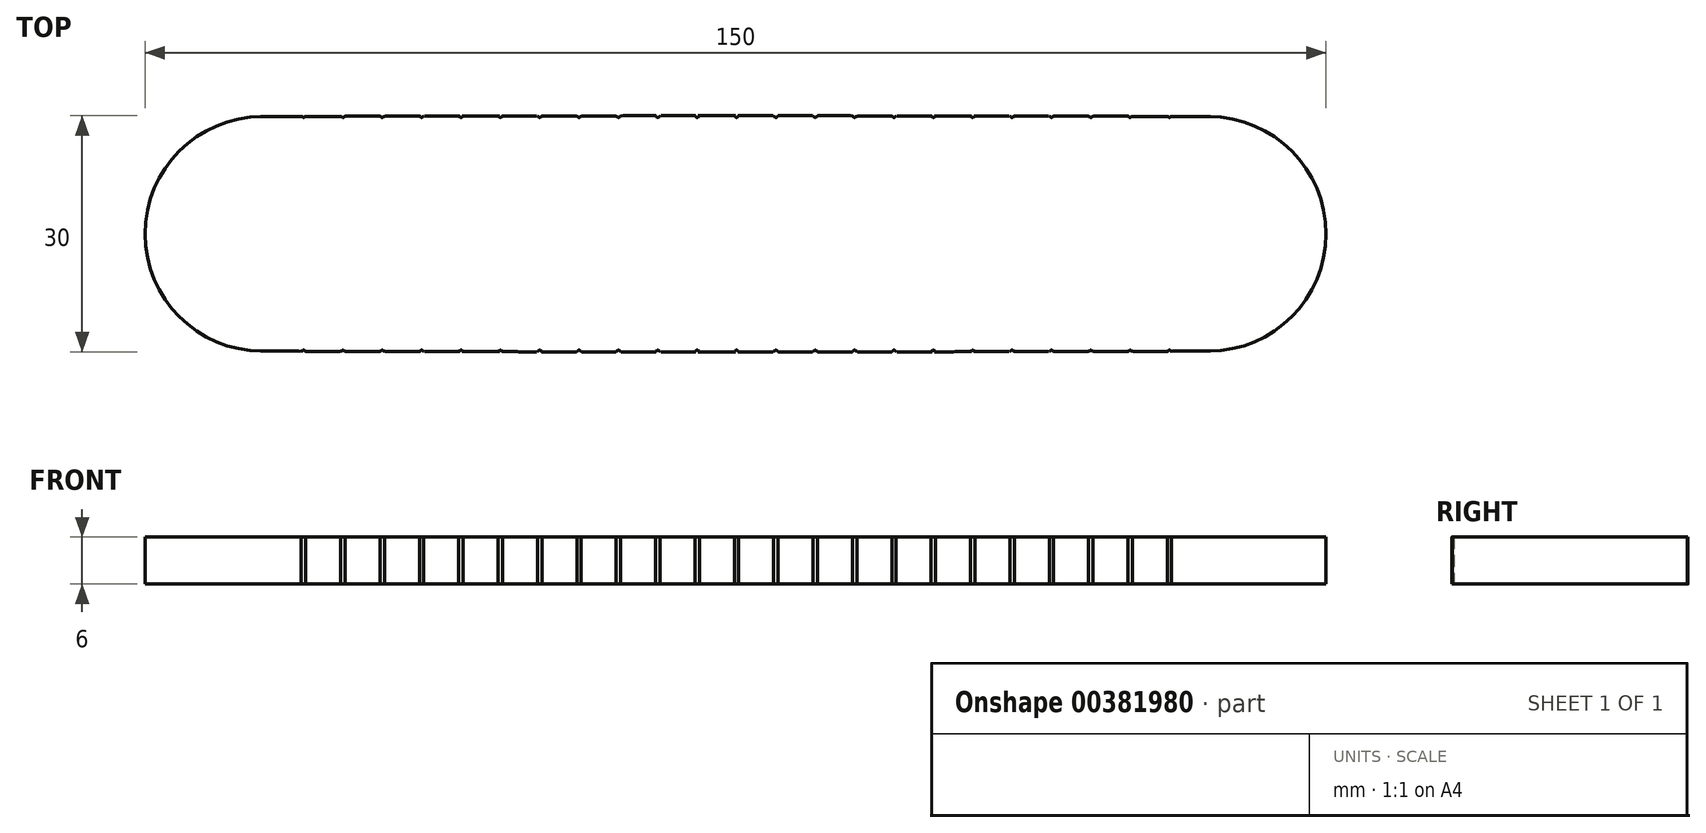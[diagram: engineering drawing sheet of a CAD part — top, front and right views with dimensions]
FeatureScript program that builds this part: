
annotation { "Feature Type Name" : "Feature", "Feature Type Description" : "" }
export const myFeature = defineFeature(function(context is Context, id is Id, definition is map)
    precondition{}
    {
        {
            var Q0;
            Q0=qCreatedBy(makeId("Top.planeOp"),FACE);
            var sketch = newSketch(context, id + "F0", { "sketchPlane" : qUnion([Q0])});
            skArc(sketch, "E0", {"start": v(0, 15) * mm, "mid": v(-30.07, 14.97) * mm, "end": v(-60.15, 14.9) * mm});
            skArc(sketch, "E1", {"start": v(-60.15, 14.9) * mm, "mid": v(-70.65, 10.52) * mm, "end": v(-75, 0) * mm});
            skLineSegment(sketch, "E2", {"start": v(0, 15) * mm, "end": v(78.08, 15) * mm, "construction": true});
            skLineSegment(sketch, "E3", {"start": v(0, 15) * mm, "end": v(0, -40.36) * mm, "construction": true});
            skLineSegment(sketch, "E4", {"start": v(-60.1, 0) * mm, "end": v(-3.88, 0) * mm, "construction": true});
            skArc(sketch, "E5.MirrorCS", {"start": v(0, 15) * mm, "mid": v(30.07, 14.97) * mm, "end": v(60.15, 14.9) * mm});
            skArc(sketch, "E6.MirrorCS", {"start": v(60.15, 14.9) * mm, "mid": v(70.65, 10.52) * mm, "end": v(75, 0) * mm});
            skArc(sketch, "E7.MirrorCS", {"start": v(0, -15) * mm, "mid": v(-30.07, -14.97) * mm, "end": v(-60.15, -14.9) * mm});
            skArc(sketch, "E8.MirrorCS", {"start": v(0, -15) * mm, "mid": v(30.07, -14.97) * mm, "end": v(60.15, -14.9) * mm});
            skArc(sketch, "E9.MirrorCS", {"start": v(60.15, -14.9) * mm, "mid": v(70.65, -10.52) * mm, "end": v(75, 0) * mm});
            skArc(sketch, "E10.MirrorCS", {"start": v(-60.15, -14.9) * mm, "mid": v(-70.65, -10.52) * mm, "end": v(-75, 0) * mm});
            skSolve(sketch);
        }
        {
            var Q0;
            Q0 = qSketchRegion(id + "F0", true);
            extrude(context, id + "F1", {"entities" : qUnion([Q0]), "depth" : 6 * mm});
        }
        {
            var Q0;
            Q0=qCreatedBy(makeId("Top.planeOp"),FACE);
            var sketch = newSketch(context, id + "F2", { "sketchPlane" : qUnion([Q0])});
            skArc(sketch, "E11", {"start": v(-54.93, 14.8) * mm, "mid": v(-55.03, 14.87) * mm, "end": v(-55.15, 14.9) * mm});
            skArc(sketch, "E12", {"start": v(-54.93, 14.8) * mm, "mid": v(-54.87, 14.77) * mm, "end": v(-54.81, 14.8) * mm});
            skArc(sketch, "E13", {"start": v(-54.81, 14.8) * mm, "mid": v(-54.71, 14.87) * mm, "end": v(-54.6, 14.9) * mm});
            skLineSegment(sketch, "E14", {"start": v(-55.15, 14.9) * mm, "end": v(-49.73, 14.9) * mm, "construction": true});
            skLineSegment(sketch, "E15", {"start": v(-54.6, 14.9) * mm, "end": v(-47.2, 14.9) * mm, "construction": true});
            skLineSegment(sketch, "E16", {"start": v(-55.15, 14.9) * mm, "end": v(-55.15, 15.28) * mm});
            skLineSegment(sketch, "E17", {"start": v(-55.15, 15.28) * mm, "end": v(-54.6, 15.28) * mm});
            skLineSegment(sketch, "E18", {"start": v(-54.6, 15.28) * mm, "end": v(-54.6, 14.9) * mm});
            skArc(sketch, "E19.MirrorCS", {"start": v(-54.93, -14.8) * mm, "mid": v(-55.03, -14.87) * mm, "end": v(-55.15, -14.9) * mm});
            skArc(sketch, "E20.MirrorCS", {"start": v(-54.93, -14.8) * mm, "mid": v(-54.87, -14.77) * mm, "end": v(-54.81, -14.8) * mm});
            skArc(sketch, "E21.MirrorCS", {"start": v(-54.81, -14.8) * mm, "mid": v(-54.71, -14.87) * mm, "end": v(-54.6, -14.9) * mm});
            skLineSegment(sketch, "E22.MirrorCS", {"start": v(-55.15, -14.9) * mm, "end": v(-55.15, -15.28) * mm});
            skLineSegment(sketch, "E23.MirrorCS", {"start": v(-55.15, -15.28) * mm, "end": v(-54.6, -15.28) * mm});
            skLineSegment(sketch, "E24.MirrorCS", {"start": v(-54.6, -15.28) * mm, "end": v(-54.6, -14.9) * mm});
            skLineSegment(sketch, "E25.1.0.0", {"start": v(-50.15, -15.28) * mm, "end": v(-49.6, -15.28) * mm});
            skLineSegment(sketch, "E25.1.0.1", {"start": v(-49.6, -15.28) * mm, "end": v(-49.6, -14.9) * mm});
            skLineSegment(sketch, "E25.1.0.2", {"start": v(-50.15, -14.9) * mm, "end": v(-50.15, -15.28) * mm});
            skArc(sketch, "E25.1.0.3", {"start": v(-49.81, -14.8) * mm, "mid": v(-49.71, -14.87) * mm, "end": v(-49.6, -14.9) * mm});
            skArc(sketch, "E25.1.0.4", {"start": v(-49.93, -14.8) * mm, "mid": v(-49.87, -14.77) * mm, "end": v(-49.81, -14.8) * mm});
            skArc(sketch, "E25.1.0.5", {"start": v(-49.93, 14.8) * mm, "mid": v(-50.03, 14.87) * mm, "end": v(-50.15, 14.9) * mm});
            skArc(sketch, "E25.1.0.6", {"start": v(-49.93, 14.8) * mm, "mid": v(-49.87, 14.77) * mm, "end": v(-49.81, 14.8) * mm});
            skArc(sketch, "E25.1.0.7", {"start": v(-49.81, 14.8) * mm, "mid": v(-49.71, 14.87) * mm, "end": v(-49.6, 14.9) * mm});
            skArc(sketch, "E25.1.0.8", {"start": v(-49.93, -14.8) * mm, "mid": v(-50.03, -14.87) * mm, "end": v(-50.15, -14.9) * mm});
            skLineSegment(sketch, "E25.1.0.9", {"start": v(-49.6, 15.28) * mm, "end": v(-49.6, 14.9) * mm});
            skLineSegment(sketch, "E25.1.0.10", {"start": v(-50.15, 14.9) * mm, "end": v(-50.15, 15.28) * mm});
            skLineSegment(sketch, "E25.1.0.11", {"start": v(-50.15, 15.28) * mm, "end": v(-49.6, 15.28) * mm});
            skLineSegment(sketch, "E25.2.0.0", {"start": v(-45.15, -15.28) * mm, "end": v(-44.6, -15.28) * mm});
            skLineSegment(sketch, "E25.2.0.1", {"start": v(-44.6, -15.28) * mm, "end": v(-44.6, -14.9) * mm});
            skLineSegment(sketch, "E25.2.0.2", {"start": v(-45.15, -14.9) * mm, "end": v(-45.15, -15.28) * mm});
            skArc(sketch, "E25.2.0.3", {"start": v(-44.81, -14.8) * mm, "mid": v(-44.71, -14.87) * mm, "end": v(-44.6, -14.9) * mm});
            skArc(sketch, "E25.2.0.4", {"start": v(-44.93, -14.8) * mm, "mid": v(-44.87, -14.77) * mm, "end": v(-44.81, -14.8) * mm});
            skArc(sketch, "E25.2.0.5", {"start": v(-44.93, 14.8) * mm, "mid": v(-45.03, 14.87) * mm, "end": v(-45.15, 14.9) * mm});
            skArc(sketch, "E25.2.0.6", {"start": v(-44.93, 14.8) * mm, "mid": v(-44.87, 14.77) * mm, "end": v(-44.81, 14.8) * mm});
            skArc(sketch, "E25.2.0.7", {"start": v(-44.81, 14.8) * mm, "mid": v(-44.71, 14.87) * mm, "end": v(-44.6, 14.9) * mm});
            skArc(sketch, "E25.2.0.8", {"start": v(-44.93, -14.8) * mm, "mid": v(-45.03, -14.87) * mm, "end": v(-45.15, -14.9) * mm});
            skLineSegment(sketch, "E25.2.0.9", {"start": v(-44.6, 15.28) * mm, "end": v(-44.6, 14.9) * mm});
            skLineSegment(sketch, "E25.2.0.10", {"start": v(-45.15, 14.9) * mm, "end": v(-45.15, 15.28) * mm});
            skLineSegment(sketch, "E25.2.0.11", {"start": v(-45.15, 15.28) * mm, "end": v(-44.6, 15.28) * mm});
            skLineSegment(sketch, "E25.3.0.0", {"start": v(-40.15, -15.28) * mm, "end": v(-39.6, -15.28) * mm});
            skLineSegment(sketch, "E25.3.0.1", {"start": v(-39.6, -15.28) * mm, "end": v(-39.6, -14.9) * mm});
            skLineSegment(sketch, "E25.3.0.2", {"start": v(-40.15, -14.9) * mm, "end": v(-40.15, -15.28) * mm});
            skArc(sketch, "E25.3.0.3", {"start": v(-39.81, -14.8) * mm, "mid": v(-39.71, -14.87) * mm, "end": v(-39.6, -14.9) * mm});
            skArc(sketch, "E25.3.0.4", {"start": v(-39.93, -14.8) * mm, "mid": v(-39.87, -14.77) * mm, "end": v(-39.81, -14.8) * mm});
            skArc(sketch, "E25.3.0.5", {"start": v(-39.93, 14.8) * mm, "mid": v(-40.03, 14.87) * mm, "end": v(-40.15, 14.9) * mm});
            skArc(sketch, "E25.3.0.6", {"start": v(-39.93, 14.8) * mm, "mid": v(-39.87, 14.77) * mm, "end": v(-39.81, 14.8) * mm});
            skArc(sketch, "E25.3.0.7", {"start": v(-39.81, 14.8) * mm, "mid": v(-39.71, 14.87) * mm, "end": v(-39.6, 14.9) * mm});
            skArc(sketch, "E25.3.0.8", {"start": v(-39.93, -14.8) * mm, "mid": v(-40.03, -14.87) * mm, "end": v(-40.15, -14.9) * mm});
            skLineSegment(sketch, "E25.3.0.9", {"start": v(-39.6, 15.28) * mm, "end": v(-39.6, 14.9) * mm});
            skLineSegment(sketch, "E25.3.0.10", {"start": v(-40.15, 14.9) * mm, "end": v(-40.15, 15.28) * mm});
            skLineSegment(sketch, "E25.3.0.11", {"start": v(-40.15, 15.28) * mm, "end": v(-39.6, 15.28) * mm});
            skLineSegment(sketch, "E25.4.0.0", {"start": v(-35.15, -15.28) * mm, "end": v(-34.6, -15.28) * mm});
            skLineSegment(sketch, "E25.4.0.1", {"start": v(-34.6, -15.28) * mm, "end": v(-34.6, -14.9) * mm});
            skLineSegment(sketch, "E25.4.0.2", {"start": v(-35.15, -14.9) * mm, "end": v(-35.15, -15.28) * mm});
            skArc(sketch, "E25.4.0.3", {"start": v(-34.81, -14.8) * mm, "mid": v(-34.71, -14.87) * mm, "end": v(-34.6, -14.9) * mm});
            skArc(sketch, "E25.4.0.4", {"start": v(-34.93, -14.8) * mm, "mid": v(-34.87, -14.77) * mm, "end": v(-34.81, -14.8) * mm});
            skArc(sketch, "E25.4.0.5", {"start": v(-34.93, 14.8) * mm, "mid": v(-35.03, 14.87) * mm, "end": v(-35.15, 14.9) * mm});
            skArc(sketch, "E25.4.0.6", {"start": v(-34.93, 14.8) * mm, "mid": v(-34.87, 14.77) * mm, "end": v(-34.81, 14.8) * mm});
            skArc(sketch, "E25.4.0.7", {"start": v(-34.81, 14.8) * mm, "mid": v(-34.71, 14.87) * mm, "end": v(-34.6, 14.9) * mm});
            skArc(sketch, "E25.4.0.8", {"start": v(-34.93, -14.8) * mm, "mid": v(-35.03, -14.87) * mm, "end": v(-35.15, -14.9) * mm});
            skLineSegment(sketch, "E25.4.0.9", {"start": v(-34.6, 15.28) * mm, "end": v(-34.6, 14.9) * mm});
            skLineSegment(sketch, "E25.4.0.10", {"start": v(-35.15, 14.9) * mm, "end": v(-35.15, 15.28) * mm});
            skLineSegment(sketch, "E25.4.0.11", {"start": v(-35.15, 15.28) * mm, "end": v(-34.6, 15.28) * mm});
            skLineSegment(sketch, "E25.5.0.0", {"start": v(-30.15, -15.28) * mm, "end": v(-29.6, -15.28) * mm});
            skLineSegment(sketch, "E25.5.0.1", {"start": v(-29.6, -15.28) * mm, "end": v(-29.6, -14.9) * mm});
            skLineSegment(sketch, "E25.5.0.2", {"start": v(-30.15, -14.9) * mm, "end": v(-30.15, -15.28) * mm});
            skArc(sketch, "E25.5.0.3", {"start": v(-29.81, -14.8) * mm, "mid": v(-29.71, -14.87) * mm, "end": v(-29.6, -14.9) * mm});
            skArc(sketch, "E25.5.0.4", {"start": v(-29.93, -14.8) * mm, "mid": v(-29.87, -14.77) * mm, "end": v(-29.81, -14.8) * mm});
            skArc(sketch, "E25.5.0.5", {"start": v(-29.93, 14.8) * mm, "mid": v(-30.03, 14.87) * mm, "end": v(-30.15, 14.9) * mm});
            skArc(sketch, "E25.5.0.6", {"start": v(-29.93, 14.8) * mm, "mid": v(-29.87, 14.77) * mm, "end": v(-29.81, 14.8) * mm});
            skArc(sketch, "E25.5.0.7", {"start": v(-29.81, 14.8) * mm, "mid": v(-29.71, 14.87) * mm, "end": v(-29.6, 14.9) * mm});
            skArc(sketch, "E25.5.0.8", {"start": v(-29.93, -14.8) * mm, "mid": v(-30.03, -14.87) * mm, "end": v(-30.15, -14.9) * mm});
            skLineSegment(sketch, "E25.5.0.9", {"start": v(-29.6, 15.28) * mm, "end": v(-29.6, 14.9) * mm});
            skLineSegment(sketch, "E25.5.0.10", {"start": v(-30.15, 14.9) * mm, "end": v(-30.15, 15.28) * mm});
            skLineSegment(sketch, "E25.5.0.11", {"start": v(-30.15, 15.28) * mm, "end": v(-29.6, 15.28) * mm});
            skLineSegment(sketch, "E25.6.0.0", {"start": v(-25.15, -15.28) * mm, "end": v(-24.6, -15.28) * mm});
            skLineSegment(sketch, "E25.6.0.1", {"start": v(-24.6, -15.28) * mm, "end": v(-24.6, -14.9) * mm});
            skLineSegment(sketch, "E25.6.0.2", {"start": v(-25.15, -14.9) * mm, "end": v(-25.15, -15.28) * mm});
            skArc(sketch, "E25.6.0.3", {"start": v(-24.81, -14.8) * mm, "mid": v(-24.71, -14.87) * mm, "end": v(-24.6, -14.9) * mm});
            skArc(sketch, "E25.6.0.4", {"start": v(-24.93, -14.8) * mm, "mid": v(-24.87, -14.77) * mm, "end": v(-24.81, -14.8) * mm});
            skArc(sketch, "E25.6.0.5", {"start": v(-24.93, 14.8) * mm, "mid": v(-25.03, 14.87) * mm, "end": v(-25.15, 14.9) * mm});
            skArc(sketch, "E25.6.0.6", {"start": v(-24.93, 14.8) * mm, "mid": v(-24.87, 14.77) * mm, "end": v(-24.81, 14.8) * mm});
            skArc(sketch, "E25.6.0.7", {"start": v(-24.81, 14.8) * mm, "mid": v(-24.71, 14.87) * mm, "end": v(-24.6, 14.9) * mm});
            skArc(sketch, "E25.6.0.8", {"start": v(-24.93, -14.8) * mm, "mid": v(-25.03, -14.87) * mm, "end": v(-25.15, -14.9) * mm});
            skLineSegment(sketch, "E25.6.0.9", {"start": v(-24.6, 15.28) * mm, "end": v(-24.6, 14.9) * mm});
            skLineSegment(sketch, "E25.6.0.10", {"start": v(-25.15, 14.9) * mm, "end": v(-25.15, 15.28) * mm});
            skLineSegment(sketch, "E25.6.0.11", {"start": v(-25.15, 15.28) * mm, "end": v(-24.6, 15.28) * mm});
            skLineSegment(sketch, "E25.7.0.0", {"start": v(-20.15, -15.28) * mm, "end": v(-19.6, -15.28) * mm});
            skLineSegment(sketch, "E25.7.0.1", {"start": v(-19.6, -15.28) * mm, "end": v(-19.6, -14.9) * mm});
            skLineSegment(sketch, "E25.7.0.2", {"start": v(-20.15, -14.9) * mm, "end": v(-20.15, -15.28) * mm});
            skArc(sketch, "E25.7.0.3", {"start": v(-19.81, -14.8) * mm, "mid": v(-19.71, -14.87) * mm, "end": v(-19.6, -14.9) * mm});
            skArc(sketch, "E25.7.0.4", {"start": v(-19.93, -14.8) * mm, "mid": v(-19.87, -14.77) * mm, "end": v(-19.81, -14.8) * mm});
            skArc(sketch, "E25.7.0.5", {"start": v(-19.93, 14.8) * mm, "mid": v(-20.03, 14.87) * mm, "end": v(-20.15, 14.9) * mm});
            skArc(sketch, "E25.7.0.6", {"start": v(-19.93, 14.8) * mm, "mid": v(-19.87, 14.77) * mm, "end": v(-19.81, 14.8) * mm});
            skArc(sketch, "E25.7.0.7", {"start": v(-19.81, 14.8) * mm, "mid": v(-19.71, 14.87) * mm, "end": v(-19.6, 14.9) * mm});
            skArc(sketch, "E25.7.0.8", {"start": v(-19.93, -14.8) * mm, "mid": v(-20.03, -14.87) * mm, "end": v(-20.15, -14.9) * mm});
            skLineSegment(sketch, "E25.7.0.9", {"start": v(-19.6, 15.28) * mm, "end": v(-19.6, 14.9) * mm});
            skLineSegment(sketch, "E25.7.0.10", {"start": v(-20.15, 14.9) * mm, "end": v(-20.15, 15.28) * mm});
            skLineSegment(sketch, "E25.7.0.11", {"start": v(-20.15, 15.28) * mm, "end": v(-19.6, 15.28) * mm});
            skLineSegment(sketch, "E25.8.0.0", {"start": v(-15.15, -15.28) * mm, "end": v(-14.6, -15.28) * mm});
            skLineSegment(sketch, "E25.8.0.1", {"start": v(-14.6, -15.28) * mm, "end": v(-14.6, -14.9) * mm});
            skLineSegment(sketch, "E25.8.0.2", {"start": v(-15.15, -14.9) * mm, "end": v(-15.15, -15.28) * mm});
            skArc(sketch, "E25.8.0.3", {"start": v(-14.81, -14.8) * mm, "mid": v(-14.71, -14.87) * mm, "end": v(-14.6, -14.9) * mm});
            skArc(sketch, "E25.8.0.4", {"start": v(-14.93, -14.8) * mm, "mid": v(-14.87, -14.77) * mm, "end": v(-14.81, -14.8) * mm});
            skArc(sketch, "E25.8.0.5", {"start": v(-14.93, 14.8) * mm, "mid": v(-15.03, 14.87) * mm, "end": v(-15.15, 14.9) * mm});
            skArc(sketch, "E25.8.0.6", {"start": v(-14.93, 14.8) * mm, "mid": v(-14.87, 14.77) * mm, "end": v(-14.81, 14.8) * mm});
            skArc(sketch, "E25.8.0.7", {"start": v(-14.81, 14.8) * mm, "mid": v(-14.71, 14.87) * mm, "end": v(-14.6, 14.9) * mm});
            skArc(sketch, "E25.8.0.8", {"start": v(-14.93, -14.8) * mm, "mid": v(-15.03, -14.87) * mm, "end": v(-15.15, -14.9) * mm});
            skLineSegment(sketch, "E25.8.0.9", {"start": v(-14.6, 15.28) * mm, "end": v(-14.6, 14.9) * mm});
            skLineSegment(sketch, "E25.8.0.10", {"start": v(-15.15, 14.9) * mm, "end": v(-15.15, 15.28) * mm});
            skLineSegment(sketch, "E25.8.0.11", {"start": v(-15.15, 15.28) * mm, "end": v(-14.6, 15.28) * mm});
            skLineSegment(sketch, "E25.9.0.0", {"start": v(-10.15, -15.28) * mm, "end": v(-9.6, -15.28) * mm});
            skLineSegment(sketch, "E25.9.0.1", {"start": v(-9.6, -15.28) * mm, "end": v(-9.6, -14.9) * mm});
            skLineSegment(sketch, "E25.9.0.2", {"start": v(-10.15, -14.9) * mm, "end": v(-10.15, -15.28) * mm});
            skArc(sketch, "E25.9.0.3", {"start": v(-9.81, -14.8) * mm, "mid": v(-9.71, -14.87) * mm, "end": v(-9.6, -14.9) * mm});
            skArc(sketch, "E25.9.0.4", {"start": v(-9.93, -14.8) * mm, "mid": v(-9.87, -14.77) * mm, "end": v(-9.81, -14.8) * mm});
            skArc(sketch, "E25.9.0.5", {"start": v(-9.93, 14.8) * mm, "mid": v(-10.03, 14.87) * mm, "end": v(-10.15, 14.9) * mm});
            skArc(sketch, "E25.9.0.6", {"start": v(-9.93, 14.8) * mm, "mid": v(-9.87, 14.77) * mm, "end": v(-9.81, 14.8) * mm});
            skArc(sketch, "E25.9.0.7", {"start": v(-9.81, 14.8) * mm, "mid": v(-9.71, 14.87) * mm, "end": v(-9.6, 14.9) * mm});
            skArc(sketch, "E25.9.0.8", {"start": v(-9.93, -14.8) * mm, "mid": v(-10.03, -14.87) * mm, "end": v(-10.15, -14.9) * mm});
            skLineSegment(sketch, "E25.9.0.9", {"start": v(-9.6, 15.28) * mm, "end": v(-9.6, 14.9) * mm});
            skLineSegment(sketch, "E25.9.0.10", {"start": v(-10.15, 14.9) * mm, "end": v(-10.15, 15.28) * mm});
            skLineSegment(sketch, "E25.9.0.11", {"start": v(-10.15, 15.28) * mm, "end": v(-9.6, 15.28) * mm});
            skLineSegment(sketch, "E25.10.0.0", {"start": v(-5.15, -15.28) * mm, "end": v(-4.6, -15.28) * mm});
            skLineSegment(sketch, "E25.10.0.1", {"start": v(-4.6, -15.28) * mm, "end": v(-4.6, -14.9) * mm});
            skLineSegment(sketch, "E25.10.0.2", {"start": v(-5.15, -14.9) * mm, "end": v(-5.15, -15.28) * mm});
            skArc(sketch, "E25.10.0.3", {"start": v(-4.81, -14.8) * mm, "mid": v(-4.71, -14.87) * mm, "end": v(-4.6, -14.9) * mm});
            skArc(sketch, "E25.10.0.4", {"start": v(-4.93, -14.8) * mm, "mid": v(-4.87, -14.77) * mm, "end": v(-4.81, -14.8) * mm});
            skArc(sketch, "E25.10.0.5", {"start": v(-4.93, 14.8) * mm, "mid": v(-5.03, 14.87) * mm, "end": v(-5.15, 14.9) * mm});
            skArc(sketch, "E25.10.0.6", {"start": v(-4.93, 14.8) * mm, "mid": v(-4.87, 14.77) * mm, "end": v(-4.81, 14.8) * mm});
            skArc(sketch, "E25.10.0.7", {"start": v(-4.81, 14.8) * mm, "mid": v(-4.71, 14.87) * mm, "end": v(-4.6, 14.9) * mm});
            skArc(sketch, "E25.10.0.8", {"start": v(-4.93, -14.8) * mm, "mid": v(-5.03, -14.87) * mm, "end": v(-5.15, -14.9) * mm});
            skLineSegment(sketch, "E25.10.0.9", {"start": v(-4.6, 15.28) * mm, "end": v(-4.6, 14.9) * mm});
            skLineSegment(sketch, "E25.10.0.10", {"start": v(-5.15, 14.9) * mm, "end": v(-5.15, 15.28) * mm});
            skLineSegment(sketch, "E25.10.0.11", {"start": v(-5.15, 15.28) * mm, "end": v(-4.6, 15.28) * mm});
            skLineSegment(sketch, "E25.11.0.0", {"start": v(-0.15, -15.28) * mm, "end": v(0.4, -15.28) * mm});
            skLineSegment(sketch, "E25.11.0.1", {"start": v(0.4, -15.28) * mm, "end": v(0.4, -14.9) * mm});
            skLineSegment(sketch, "E25.11.0.2", {"start": v(-0.15, -14.9) * mm, "end": v(-0.15, -15.28) * mm});
            skArc(sketch, "E25.11.0.3", {"start": v(0.19, -14.8) * mm, "mid": v(0.29, -14.87) * mm, "end": v(0.4, -14.9) * mm});
            skArc(sketch, "E25.11.0.4", {"start": v(0.07, -14.8) * mm, "mid": v(0.13, -14.77) * mm, "end": v(0.19, -14.8) * mm});
            skArc(sketch, "E25.11.0.5", {"start": v(0.07, 14.8) * mm, "mid": v(-0.03, 14.87) * mm, "end": v(-0.15, 14.9) * mm});
            skArc(sketch, "E25.11.0.6", {"start": v(0.07, 14.8) * mm, "mid": v(0.13, 14.77) * mm, "end": v(0.19, 14.8) * mm});
            skArc(sketch, "E25.11.0.7", {"start": v(0.19, 14.8) * mm, "mid": v(0.29, 14.87) * mm, "end": v(0.4, 14.9) * mm});
            skArc(sketch, "E25.11.0.8", {"start": v(0.07, -14.8) * mm, "mid": v(-0.03, -14.87) * mm, "end": v(-0.15, -14.9) * mm});
            skLineSegment(sketch, "E25.11.0.9", {"start": v(0.4, 15.28) * mm, "end": v(0.4, 14.9) * mm});
            skLineSegment(sketch, "E25.11.0.10", {"start": v(-0.15, 14.9) * mm, "end": v(-0.15, 15.28) * mm});
            skLineSegment(sketch, "E25.11.0.11", {"start": v(-0.15, 15.28) * mm, "end": v(0.4, 15.28) * mm});
            skLineSegment(sketch, "E25.12.0.0", {"start": v(4.85, -15.28) * mm, "end": v(5.4, -15.28) * mm});
            skLineSegment(sketch, "E25.12.0.1", {"start": v(5.4, -15.28) * mm, "end": v(5.4, -14.9) * mm});
            skLineSegment(sketch, "E25.12.0.2", {"start": v(4.85, -14.9) * mm, "end": v(4.85, -15.28) * mm});
            skArc(sketch, "E25.12.0.3", {"start": v(5.19, -14.8) * mm, "mid": v(5.29, -14.87) * mm, "end": v(5.4, -14.9) * mm});
            skArc(sketch, "E25.12.0.4", {"start": v(5.07, -14.8) * mm, "mid": v(5.13, -14.77) * mm, "end": v(5.19, -14.8) * mm});
            skArc(sketch, "E25.12.0.5", {"start": v(5.07, 14.8) * mm, "mid": v(4.97, 14.87) * mm, "end": v(4.85, 14.9) * mm});
            skArc(sketch, "E25.12.0.6", {"start": v(5.07, 14.8) * mm, "mid": v(5.13, 14.77) * mm, "end": v(5.19, 14.8) * mm});
            skArc(sketch, "E25.12.0.7", {"start": v(5.19, 14.8) * mm, "mid": v(5.29, 14.87) * mm, "end": v(5.4, 14.9) * mm});
            skArc(sketch, "E25.12.0.8", {"start": v(5.07, -14.8) * mm, "mid": v(4.97, -14.87) * mm, "end": v(4.85, -14.9) * mm});
            skLineSegment(sketch, "E25.12.0.9", {"start": v(5.4, 15.28) * mm, "end": v(5.4, 14.9) * mm});
            skLineSegment(sketch, "E25.12.0.10", {"start": v(4.85, 14.9) * mm, "end": v(4.85, 15.28) * mm});
            skLineSegment(sketch, "E25.12.0.11", {"start": v(4.85, 15.28) * mm, "end": v(5.4, 15.28) * mm});
            skLineSegment(sketch, "E25.13.0.0", {"start": v(9.85, -15.28) * mm, "end": v(10.4, -15.28) * mm});
            skLineSegment(sketch, "E25.13.0.1", {"start": v(10.4, -15.28) * mm, "end": v(10.4, -14.9) * mm});
            skLineSegment(sketch, "E25.13.0.2", {"start": v(9.85, -14.9) * mm, "end": v(9.85, -15.28) * mm});
            skArc(sketch, "E25.13.0.3", {"start": v(10.19, -14.8) * mm, "mid": v(10.29, -14.87) * mm, "end": v(10.4, -14.9) * mm});
            skArc(sketch, "E25.13.0.4", {"start": v(10.07, -14.8) * mm, "mid": v(10.13, -14.77) * mm, "end": v(10.19, -14.8) * mm});
            skArc(sketch, "E25.13.0.5", {"start": v(10.07, 14.8) * mm, "mid": v(9.97, 14.87) * mm, "end": v(9.85, 14.9) * mm});
            skArc(sketch, "E25.13.0.6", {"start": v(10.07, 14.8) * mm, "mid": v(10.13, 14.77) * mm, "end": v(10.19, 14.8) * mm});
            skArc(sketch, "E25.13.0.7", {"start": v(10.19, 14.8) * mm, "mid": v(10.29, 14.87) * mm, "end": v(10.4, 14.9) * mm});
            skArc(sketch, "E25.13.0.8", {"start": v(10.07, -14.8) * mm, "mid": v(9.97, -14.87) * mm, "end": v(9.85, -14.9) * mm});
            skLineSegment(sketch, "E25.13.0.9", {"start": v(10.4, 15.28) * mm, "end": v(10.4, 14.9) * mm});
            skLineSegment(sketch, "E25.13.0.10", {"start": v(9.85, 14.9) * mm, "end": v(9.85, 15.28) * mm});
            skLineSegment(sketch, "E25.13.0.11", {"start": v(9.85, 15.28) * mm, "end": v(10.4, 15.28) * mm});
            skLineSegment(sketch, "E25.14.0.0", {"start": v(14.85, -15.28) * mm, "end": v(15.4, -15.28) * mm});
            skLineSegment(sketch, "E25.14.0.1", {"start": v(15.4, -15.28) * mm, "end": v(15.4, -14.9) * mm});
            skLineSegment(sketch, "E25.14.0.2", {"start": v(14.85, -14.9) * mm, "end": v(14.85, -15.28) * mm});
            skArc(sketch, "E25.14.0.3", {"start": v(15.19, -14.8) * mm, "mid": v(15.29, -14.87) * mm, "end": v(15.4, -14.9) * mm});
            skArc(sketch, "E25.14.0.4", {"start": v(15.07, -14.8) * mm, "mid": v(15.13, -14.77) * mm, "end": v(15.19, -14.8) * mm});
            skArc(sketch, "E25.14.0.5", {"start": v(15.07, 14.8) * mm, "mid": v(14.97, 14.87) * mm, "end": v(14.85, 14.9) * mm});
            skArc(sketch, "E25.14.0.6", {"start": v(15.07, 14.8) * mm, "mid": v(15.13, 14.77) * mm, "end": v(15.19, 14.8) * mm});
            skArc(sketch, "E25.14.0.7", {"start": v(15.19, 14.8) * mm, "mid": v(15.29, 14.87) * mm, "end": v(15.4, 14.9) * mm});
            skArc(sketch, "E25.14.0.8", {"start": v(15.07, -14.8) * mm, "mid": v(14.97, -14.87) * mm, "end": v(14.85, -14.9) * mm});
            skLineSegment(sketch, "E25.14.0.9", {"start": v(15.4, 15.28) * mm, "end": v(15.4, 14.9) * mm});
            skLineSegment(sketch, "E25.14.0.10", {"start": v(14.85, 14.9) * mm, "end": v(14.85, 15.28) * mm});
            skLineSegment(sketch, "E25.14.0.11", {"start": v(14.85, 15.28) * mm, "end": v(15.4, 15.28) * mm});
            skLineSegment(sketch, "E25.15.0.0", {"start": v(19.85, -15.28) * mm, "end": v(20.4, -15.28) * mm});
            skLineSegment(sketch, "E25.15.0.1", {"start": v(20.4, -15.28) * mm, "end": v(20.4, -14.9) * mm});
            skLineSegment(sketch, "E25.15.0.2", {"start": v(19.85, -14.9) * mm, "end": v(19.85, -15.28) * mm});
            skArc(sketch, "E25.15.0.3", {"start": v(20.19, -14.8) * mm, "mid": v(20.29, -14.87) * mm, "end": v(20.4, -14.9) * mm});
            skArc(sketch, "E25.15.0.4", {"start": v(20.07, -14.8) * mm, "mid": v(20.13, -14.77) * mm, "end": v(20.19, -14.8) * mm});
            skArc(sketch, "E25.15.0.5", {"start": v(20.07, 14.8) * mm, "mid": v(19.97, 14.87) * mm, "end": v(19.85, 14.9) * mm});
            skArc(sketch, "E25.15.0.6", {"start": v(20.07, 14.8) * mm, "mid": v(20.13, 14.77) * mm, "end": v(20.19, 14.8) * mm});
            skArc(sketch, "E25.15.0.7", {"start": v(20.19, 14.8) * mm, "mid": v(20.29, 14.87) * mm, "end": v(20.4, 14.9) * mm});
            skArc(sketch, "E25.15.0.8", {"start": v(20.07, -14.8) * mm, "mid": v(19.97, -14.87) * mm, "end": v(19.85, -14.9) * mm});
            skLineSegment(sketch, "E25.15.0.9", {"start": v(20.4, 15.28) * mm, "end": v(20.4, 14.9) * mm});
            skLineSegment(sketch, "E25.15.0.10", {"start": v(19.85, 14.9) * mm, "end": v(19.85, 15.28) * mm});
            skLineSegment(sketch, "E25.15.0.11", {"start": v(19.85, 15.28) * mm, "end": v(20.4, 15.28) * mm});
            skLineSegment(sketch, "E25.16.0.0", {"start": v(24.85, -15.28) * mm, "end": v(25.4, -15.28) * mm});
            skLineSegment(sketch, "E25.16.0.1", {"start": v(25.4, -15.28) * mm, "end": v(25.4, -14.9) * mm});
            skLineSegment(sketch, "E25.16.0.2", {"start": v(24.85, -14.9) * mm, "end": v(24.85, -15.28) * mm});
            skArc(sketch, "E25.16.0.3", {"start": v(25.19, -14.8) * mm, "mid": v(25.29, -14.87) * mm, "end": v(25.4, -14.9) * mm});
            skArc(sketch, "E25.16.0.4", {"start": v(25.07, -14.8) * mm, "mid": v(25.13, -14.77) * mm, "end": v(25.19, -14.8) * mm});
            skArc(sketch, "E25.16.0.5", {"start": v(25.07, 14.8) * mm, "mid": v(24.97, 14.87) * mm, "end": v(24.85, 14.9) * mm});
            skArc(sketch, "E25.16.0.6", {"start": v(25.07, 14.8) * mm, "mid": v(25.13, 14.77) * mm, "end": v(25.19, 14.8) * mm});
            skArc(sketch, "E25.16.0.7", {"start": v(25.19, 14.8) * mm, "mid": v(25.29, 14.87) * mm, "end": v(25.4, 14.9) * mm});
            skArc(sketch, "E25.16.0.8", {"start": v(25.07, -14.8) * mm, "mid": v(24.97, -14.87) * mm, "end": v(24.85, -14.9) * mm});
            skLineSegment(sketch, "E25.16.0.9", {"start": v(25.4, 15.28) * mm, "end": v(25.4, 14.9) * mm});
            skLineSegment(sketch, "E25.16.0.10", {"start": v(24.85, 14.9) * mm, "end": v(24.85, 15.28) * mm});
            skLineSegment(sketch, "E25.16.0.11", {"start": v(24.85, 15.28) * mm, "end": v(25.4, 15.28) * mm});
            skLineSegment(sketch, "E25.17.0.0", {"start": v(29.85, -15.28) * mm, "end": v(30.4, -15.28) * mm});
            skLineSegment(sketch, "E25.17.0.1", {"start": v(30.4, -15.28) * mm, "end": v(30.4, -14.9) * mm});
            skLineSegment(sketch, "E25.17.0.2", {"start": v(29.85, -14.9) * mm, "end": v(29.85, -15.28) * mm});
            skArc(sketch, "E25.17.0.3", {"start": v(30.19, -14.8) * mm, "mid": v(30.29, -14.87) * mm, "end": v(30.4, -14.9) * mm});
            skArc(sketch, "E25.17.0.4", {"start": v(30.07, -14.8) * mm, "mid": v(30.13, -14.77) * mm, "end": v(30.19, -14.8) * mm});
            skArc(sketch, "E25.17.0.5", {"start": v(30.07, 14.8) * mm, "mid": v(29.97, 14.87) * mm, "end": v(29.85, 14.9) * mm});
            skArc(sketch, "E25.17.0.6", {"start": v(30.07, 14.8) * mm, "mid": v(30.13, 14.77) * mm, "end": v(30.19, 14.8) * mm});
            skArc(sketch, "E25.17.0.7", {"start": v(30.19, 14.8) * mm, "mid": v(30.29, 14.87) * mm, "end": v(30.4, 14.9) * mm});
            skArc(sketch, "E25.17.0.8", {"start": v(30.07, -14.8) * mm, "mid": v(29.97, -14.87) * mm, "end": v(29.85, -14.9) * mm});
            skLineSegment(sketch, "E25.17.0.9", {"start": v(30.4, 15.28) * mm, "end": v(30.4, 14.9) * mm});
            skLineSegment(sketch, "E25.17.0.10", {"start": v(29.85, 14.9) * mm, "end": v(29.85, 15.28) * mm});
            skLineSegment(sketch, "E25.17.0.11", {"start": v(29.85, 15.28) * mm, "end": v(30.4, 15.28) * mm});
            skLineSegment(sketch, "E25.18.0.0", {"start": v(34.85, -15.28) * mm, "end": v(35.4, -15.28) * mm});
            skLineSegment(sketch, "E25.18.0.1", {"start": v(35.4, -15.28) * mm, "end": v(35.4, -14.9) * mm});
            skLineSegment(sketch, "E25.18.0.2", {"start": v(34.85, -14.9) * mm, "end": v(34.85, -15.28) * mm});
            skArc(sketch, "E25.18.0.3", {"start": v(35.19, -14.8) * mm, "mid": v(35.29, -14.87) * mm, "end": v(35.4, -14.9) * mm});
            skArc(sketch, "E25.18.0.4", {"start": v(35.07, -14.8) * mm, "mid": v(35.13, -14.77) * mm, "end": v(35.19, -14.8) * mm});
            skArc(sketch, "E25.18.0.5", {"start": v(35.07, 14.8) * mm, "mid": v(34.97, 14.87) * mm, "end": v(34.85, 14.9) * mm});
            skArc(sketch, "E25.18.0.6", {"start": v(35.07, 14.8) * mm, "mid": v(35.13, 14.77) * mm, "end": v(35.19, 14.8) * mm});
            skArc(sketch, "E25.18.0.7", {"start": v(35.19, 14.8) * mm, "mid": v(35.29, 14.87) * mm, "end": v(35.4, 14.9) * mm});
            skArc(sketch, "E25.18.0.8", {"start": v(35.07, -14.8) * mm, "mid": v(34.97, -14.87) * mm, "end": v(34.85, -14.9) * mm});
            skLineSegment(sketch, "E25.18.0.9", {"start": v(35.4, 15.28) * mm, "end": v(35.4, 14.9) * mm});
            skLineSegment(sketch, "E25.18.0.10", {"start": v(34.85, 14.9) * mm, "end": v(34.85, 15.28) * mm});
            skLineSegment(sketch, "E25.18.0.11", {"start": v(34.85, 15.28) * mm, "end": v(35.4, 15.28) * mm});
            skLineSegment(sketch, "E25.19.0.0", {"start": v(39.85, -15.28) * mm, "end": v(40.4, -15.28) * mm});
            skLineSegment(sketch, "E25.19.0.1", {"start": v(40.4, -15.28) * mm, "end": v(40.4, -14.9) * mm});
            skLineSegment(sketch, "E25.19.0.2", {"start": v(39.85, -14.9) * mm, "end": v(39.85, -15.28) * mm});
            skArc(sketch, "E25.19.0.3", {"start": v(40.19, -14.8) * mm, "mid": v(40.29, -14.87) * mm, "end": v(40.4, -14.9) * mm});
            skArc(sketch, "E25.19.0.4", {"start": v(40.07, -14.8) * mm, "mid": v(40.13, -14.77) * mm, "end": v(40.19, -14.8) * mm});
            skArc(sketch, "E25.19.0.5", {"start": v(40.07, 14.8) * mm, "mid": v(39.97, 14.87) * mm, "end": v(39.85, 14.9) * mm});
            skArc(sketch, "E25.19.0.6", {"start": v(40.07, 14.8) * mm, "mid": v(40.13, 14.77) * mm, "end": v(40.19, 14.8) * mm});
            skArc(sketch, "E25.19.0.7", {"start": v(40.19, 14.8) * mm, "mid": v(40.29, 14.87) * mm, "end": v(40.4, 14.9) * mm});
            skArc(sketch, "E25.19.0.8", {"start": v(40.07, -14.8) * mm, "mid": v(39.97, -14.87) * mm, "end": v(39.85, -14.9) * mm});
            skLineSegment(sketch, "E25.19.0.9", {"start": v(40.4, 15.28) * mm, "end": v(40.4, 14.9) * mm});
            skLineSegment(sketch, "E25.19.0.10", {"start": v(39.85, 14.9) * mm, "end": v(39.85, 15.28) * mm});
            skLineSegment(sketch, "E25.19.0.11", {"start": v(39.85, 15.28) * mm, "end": v(40.4, 15.28) * mm});
            skLineSegment(sketch, "E25.20.0.0", {"start": v(44.85, -15.28) * mm, "end": v(45.4, -15.28) * mm});
            skLineSegment(sketch, "E25.20.0.1", {"start": v(45.4, -15.28) * mm, "end": v(45.4, -14.9) * mm});
            skLineSegment(sketch, "E25.20.0.2", {"start": v(44.85, -14.9) * mm, "end": v(44.85, -15.28) * mm});
            skArc(sketch, "E25.20.0.3", {"start": v(45.19, -14.8) * mm, "mid": v(45.29, -14.87) * mm, "end": v(45.4, -14.9) * mm});
            skArc(sketch, "E25.20.0.4", {"start": v(45.07, -14.8) * mm, "mid": v(45.13, -14.77) * mm, "end": v(45.19, -14.8) * mm});
            skArc(sketch, "E25.20.0.5", {"start": v(45.07, 14.8) * mm, "mid": v(44.97, 14.87) * mm, "end": v(44.85, 14.9) * mm});
            skArc(sketch, "E25.20.0.6", {"start": v(45.07, 14.8) * mm, "mid": v(45.13, 14.77) * mm, "end": v(45.19, 14.8) * mm});
            skArc(sketch, "E25.20.0.7", {"start": v(45.19, 14.8) * mm, "mid": v(45.29, 14.87) * mm, "end": v(45.4, 14.9) * mm});
            skArc(sketch, "E25.20.0.8", {"start": v(45.07, -14.8) * mm, "mid": v(44.97, -14.87) * mm, "end": v(44.85, -14.9) * mm});
            skLineSegment(sketch, "E25.20.0.9", {"start": v(45.4, 15.28) * mm, "end": v(45.4, 14.9) * mm});
            skLineSegment(sketch, "E25.20.0.10", {"start": v(44.85, 14.9) * mm, "end": v(44.85, 15.28) * mm});
            skLineSegment(sketch, "E25.20.0.11", {"start": v(44.85, 15.28) * mm, "end": v(45.4, 15.28) * mm});
            skLineSegment(sketch, "E25.21.0.0", {"start": v(49.85, -15.28) * mm, "end": v(50.4, -15.28) * mm});
            skLineSegment(sketch, "E25.21.0.1", {"start": v(50.4, -15.28) * mm, "end": v(50.4, -14.9) * mm});
            skLineSegment(sketch, "E25.21.0.2", {"start": v(49.85, -14.9) * mm, "end": v(49.85, -15.28) * mm});
            skArc(sketch, "E25.21.0.3", {"start": v(50.19, -14.8) * mm, "mid": v(50.29, -14.87) * mm, "end": v(50.4, -14.9) * mm});
            skArc(sketch, "E25.21.0.4", {"start": v(50.07, -14.8) * mm, "mid": v(50.13, -14.77) * mm, "end": v(50.19, -14.8) * mm});
            skArc(sketch, "E25.21.0.5", {"start": v(50.07, 14.8) * mm, "mid": v(49.97, 14.87) * mm, "end": v(49.85, 14.9) * mm});
            skArc(sketch, "E25.21.0.6", {"start": v(50.07, 14.8) * mm, "mid": v(50.13, 14.77) * mm, "end": v(50.19, 14.8) * mm});
            skArc(sketch, "E25.21.0.7", {"start": v(50.19, 14.8) * mm, "mid": v(50.29, 14.87) * mm, "end": v(50.4, 14.9) * mm});
            skArc(sketch, "E25.21.0.8", {"start": v(50.07, -14.8) * mm, "mid": v(49.97, -14.87) * mm, "end": v(49.85, -14.9) * mm});
            skLineSegment(sketch, "E25.21.0.9", {"start": v(50.4, 15.28) * mm, "end": v(50.4, 14.9) * mm});
            skLineSegment(sketch, "E25.21.0.10", {"start": v(49.85, 14.9) * mm, "end": v(49.85, 15.28) * mm});
            skLineSegment(sketch, "E25.21.0.11", {"start": v(49.85, 15.28) * mm, "end": v(50.4, 15.28) * mm});
            skLineSegment(sketch, "E25.22.0.0", {"start": v(54.85, -15.28) * mm, "end": v(55.4, -15.28) * mm});
            skLineSegment(sketch, "E25.22.0.1", {"start": v(55.4, -15.28) * mm, "end": v(55.4, -14.9) * mm});
            skLineSegment(sketch, "E25.22.0.2", {"start": v(54.85, -14.9) * mm, "end": v(54.85, -15.28) * mm});
            skArc(sketch, "E25.22.0.3", {"start": v(55.19, -14.8) * mm, "mid": v(55.29, -14.87) * mm, "end": v(55.4, -14.9) * mm});
            skArc(sketch, "E25.22.0.4", {"start": v(55.07, -14.8) * mm, "mid": v(55.13, -14.77) * mm, "end": v(55.19, -14.8) * mm});
            skArc(sketch, "E25.22.0.5", {"start": v(55.07, 14.8) * mm, "mid": v(54.97, 14.87) * mm, "end": v(54.85, 14.9) * mm});
            skArc(sketch, "E25.22.0.6", {"start": v(55.07, 14.8) * mm, "mid": v(55.13, 14.77) * mm, "end": v(55.19, 14.8) * mm});
            skArc(sketch, "E25.22.0.7", {"start": v(55.19, 14.8) * mm, "mid": v(55.29, 14.87) * mm, "end": v(55.4, 14.9) * mm});
            skArc(sketch, "E25.22.0.8", {"start": v(55.07, -14.8) * mm, "mid": v(54.97, -14.87) * mm, "end": v(54.85, -14.9) * mm});
            skLineSegment(sketch, "E25.22.0.9", {"start": v(55.4, 15.28) * mm, "end": v(55.4, 14.9) * mm});
            skLineSegment(sketch, "E25.22.0.10", {"start": v(54.85, 14.9) * mm, "end": v(54.85, 15.28) * mm});
            skLineSegment(sketch, "E25.22.0.11", {"start": v(54.85, 15.28) * mm, "end": v(55.4, 15.28) * mm});
            skLineSegment(sketch, "E25.direction1", {"start": v(-55.15, -15.28) * mm, "end": v(-50.15, -15.28) * mm, "construction": true});
            skSolve(sketch);
        }
        {
            var Q0;
            Q0 = qSketchRegion(id + "F2", true);
            extrude(context, id + "F3", {"entities" : qUnion([Q0]), "operationType" : NewBodyOperationType.REMOVE, "depth" : 25 * mm});
        }
    });
